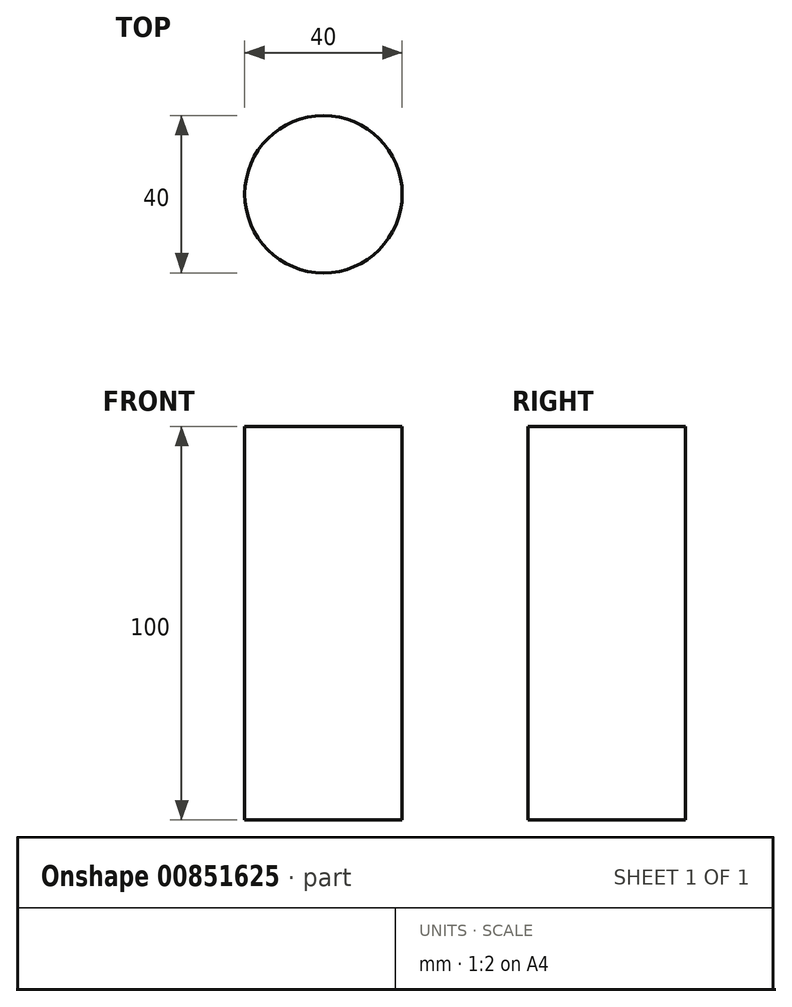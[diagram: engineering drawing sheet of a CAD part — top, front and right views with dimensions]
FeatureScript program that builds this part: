
annotation { "Feature Type Name" : "Feature", "Feature Type Description" : "" }
export const myFeature = defineFeature(function(context is Context, id is Id, definition is map)
    precondition{}
    {
        {
            var Q0;
            Q0=qCreatedBy(makeId("Top.planeOp"),FACE);
            var sketch = newSketch(context, id + "F0", { "sketchPlane" : qUnion([Q0])});
            skCircle(sketch, "E0", {"center": v(0, 0) * mm, "radius": 20 * mm});
            skSolve(sketch);
        }
        {
            var Q0;
            Q0 = qSketchRegion(id + "F0", true);
            var Q1;
            Q1 = qConstructionFilter(qBodyType(qCreatedBy(id + "F0" ,EDGE), BodyType.WIRE), ConstructionObject.NO);
            extrude(context, id + "F1", {"entities" : qUnion([Q0]), "bodyType" : ToolBodyType.SURFACE, "surfaceEntities" : qUnion([Q1]), "depth" : 100 * mm, "offsetDistance" : 25 * mm});
        }
    });
